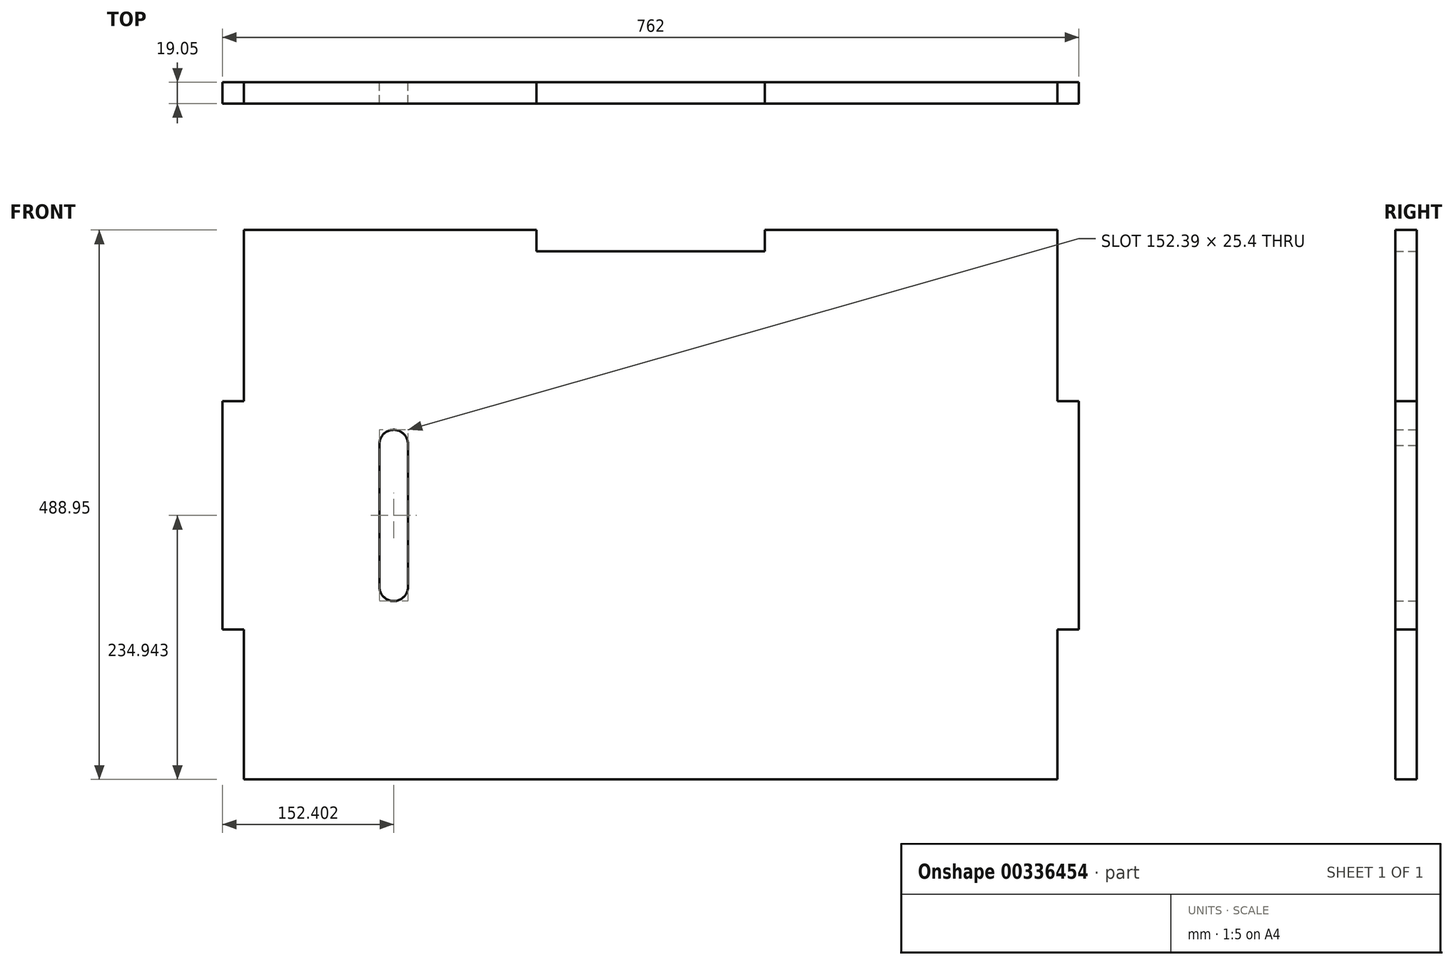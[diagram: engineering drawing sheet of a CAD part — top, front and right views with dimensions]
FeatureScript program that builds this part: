
annotation { "Feature Type Name" : "Feature", "Feature Type Description" : "" }
export const myFeature = defineFeature(function(context is Context, id is Id, definition is map)
    precondition{}
    {
        {
            var Q0;
            Q0=qCreatedBy(makeId("Front.planeOp"),FACE);
            var sketch = newSketch(context, id + "F0", { "sketchPlane" : qUnion([Q0])});
            skLineSegment(sketch, "E0.bottom", {"start": v(-444.05, 391.96) * mm, "end": v(317.95, 391.96) * mm});
            skLineSegment(sketch, "E0.top", {"start": v(-444.05, -116.04) * mm, "end": v(317.95, -116.04) * mm});
            skLineSegment(sketch, "E0.left", {"start": v(-444.05, 391.96) * mm, "end": v(-444.05, -116.04) * mm});
            skLineSegment(sketch, "E0.right", {"start": v(317.95, 391.96) * mm, "end": v(317.95, -116.04) * mm});
            skCircle(sketch, "E1", {"center": v(-291.65, 201.46) * mm, "radius": 12.7 * mm});
            skCircle(sketch, "E2", {"center": v(-291.65, 74.46) * mm, "radius": 12.7 * mm});
            skLineSegment(sketch, "E3", {"start": v(-304.35, 201.46) * mm, "end": v(-304.35, 74.46) * mm});
            skLineSegment(sketch, "E4", {"start": v(-279, 200.28) * mm, "end": v(-278.95, 74.47) * mm});
            skLineSegment(sketch, "E5.bottom", {"start": v(-425, 36.36) * mm, "end": v(-444.05, 36.36) * mm});
            skLineSegment(sketch, "E5.top", {"start": v(-425, 239.56) * mm, "end": v(-444.05, 239.56) * mm});
            skLineSegment(sketch, "E5.left", {"start": v(-425, 36.36) * mm, "end": v(-425, 239.56) * mm});
            skLineSegment(sketch, "E5.right", {"start": v(-444.05, 36.36) * mm, "end": v(-444.05, 239.56) * mm});
            skPoint(sketch, "E5.middle", {"position": v(-434.52, 137.96) * mm});
            skLineSegment(sketch, "E6", {"start": v(-425, 239.56) * mm, "end": v(-425, 391.96) * mm});
            skLineSegment(sketch, "E7", {"start": v(-425, 36.36) * mm, "end": v(-425, -116.04) * mm});
            skLineSegment(sketch, "E8.bottom", {"start": v(317.95, 36.36) * mm, "end": v(298.9, 36.36) * mm});
            skLineSegment(sketch, "E8.top", {"start": v(317.95, 239.56) * mm, "end": v(298.9, 239.56) * mm});
            skLineSegment(sketch, "E8.left", {"start": v(317.95, 36.36) * mm, "end": v(317.95, 239.56) * mm});
            skLineSegment(sketch, "E8.right", {"start": v(298.9, 36.36) * mm, "end": v(298.9, 239.56) * mm});
            skPoint(sketch, "E8.middle", {"position": v(308.43, 137.96) * mm});
            skLineSegment(sketch, "E9", {"start": v(298.9, 239.56) * mm, "end": v(298.9, 391.96) * mm});
            skLineSegment(sketch, "E10", {"start": v(298.9, 36.36) * mm, "end": v(298.9, -116.04) * mm});
            skLineSegment(sketch, "E11.bottom", {"start": v(38.55, 372.91) * mm, "end": v(-164.65, 372.91) * mm});
            skLineSegment(sketch, "E11.top", {"start": v(38.55, 391.96) * mm, "end": v(-164.65, 391.96) * mm});
            skLineSegment(sketch, "E11.left", {"start": v(38.55, 372.91) * mm, "end": v(38.55, 391.96) * mm});
            skLineSegment(sketch, "E11.right", {"start": v(-164.65, 372.91) * mm, "end": v(-164.65, 391.96) * mm});
            skPoint(sketch, "E11.middle", {"position": v(-63.05, 382.44) * mm});
            skLineSegment(sketch, "E12.bottom", {"start": v(38.55, -116.04) * mm, "end": v(-164.65, -116.04) * mm});
            skLineSegment(sketch, "E12.top", {"start": v(38.55, -96.99) * mm, "end": v(-164.65, -96.99) * mm});
            skLineSegment(sketch, "E12.left", {"start": v(38.55, -116.04) * mm, "end": v(38.55, -96.99) * mm});
            skLineSegment(sketch, "E12.right", {"start": v(-164.65, -116.04) * mm, "end": v(-164.65, -96.99) * mm});
            skPoint(sketch, "E12.middle", {"position": v(-63.05, -106.51) * mm});
            skLineSegment(sketch, "E13", {"start": v(-164.65, -96.99) * mm, "end": v(-444.05, -96.99) * mm});
            skLineSegment(sketch, "E14", {"start": v(38.55, -96.99) * mm, "end": v(317.95, -96.99) * mm});
            skSolve(sketch);
        }
        {
            var Q0;
            Q0=makeQuery(id+"F0.imprint","IMPRINT",FACE,{"disambiguationData":[TD([[makeQuery(id+"F0.imprint","IMPRINT",EDGE,{"derivedFrom":sQuery(id+"F0.wireOp",EDGE,"E5.bottom")}),-1.0]])]});
            var Q1;
            {var subQ1=sQuery(id+"F0.wireOp",EDGE,"E3");Q1=makeQuery(id+"F0.imprint","IMPRINT",FACE,{"disambiguationData":[TD([[makeQuery(id+"F0.imprint","IMPRINT",EDGE,{"derivedFrom":subQ1}),-1.0]])]});}
            var Q2;
            Q2=makeQuery(id+"F0.imprint","IMPRINT",FACE,{"disambiguationData":[TD([[makeQuery(id+"F0.imprint","IMPRINT",EDGE,{"derivedFrom":sQuery(id+"F0.wireOp",EDGE,"E8.bottom")}),-1.0]])]});
            var Q3;
            Q3=makeQuery(id+"F0.imprint","IMPRINT",FACE,{"disambiguationData":[TD([[makeQuery(id+"F0.imprint","IMPRINT",EDGE,{"derivedFrom":sQuery(id+"F0.wireOp",EDGE,"E12.bottom")}),-1.0]])]});
            extrude(context, id + "F1", {"entities" : qUnion([Q0, Q1, Q2, Q3]), "depth" : 19.05 * mm});
        }
    });
